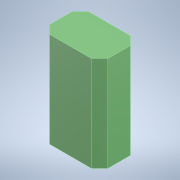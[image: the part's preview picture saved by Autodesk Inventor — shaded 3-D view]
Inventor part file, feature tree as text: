
AUTODESK INVENTOR PART (.ipt)
format: ipt  version: 2021 (Build 250183000, 183)  size: 100,864 bytes
history: native  units: mm
features: extrude x1, sketch x1
ambient origin geometry x8: Origin, YZ Plane, XZ Plane, XY Plane, X Axis, Y Axis, Z Axis, Center Point
bodies: Solid1 (feature_tree)
feature tree (2):
  extrude  "Extrusion1"  Depth=14.2mm
  sketch  "Sketch1"  dims[d0=21.2mm d1=14.2mm d2=3.0mm d3=3.0mm d10=34.4mm d11=0.0mm]
